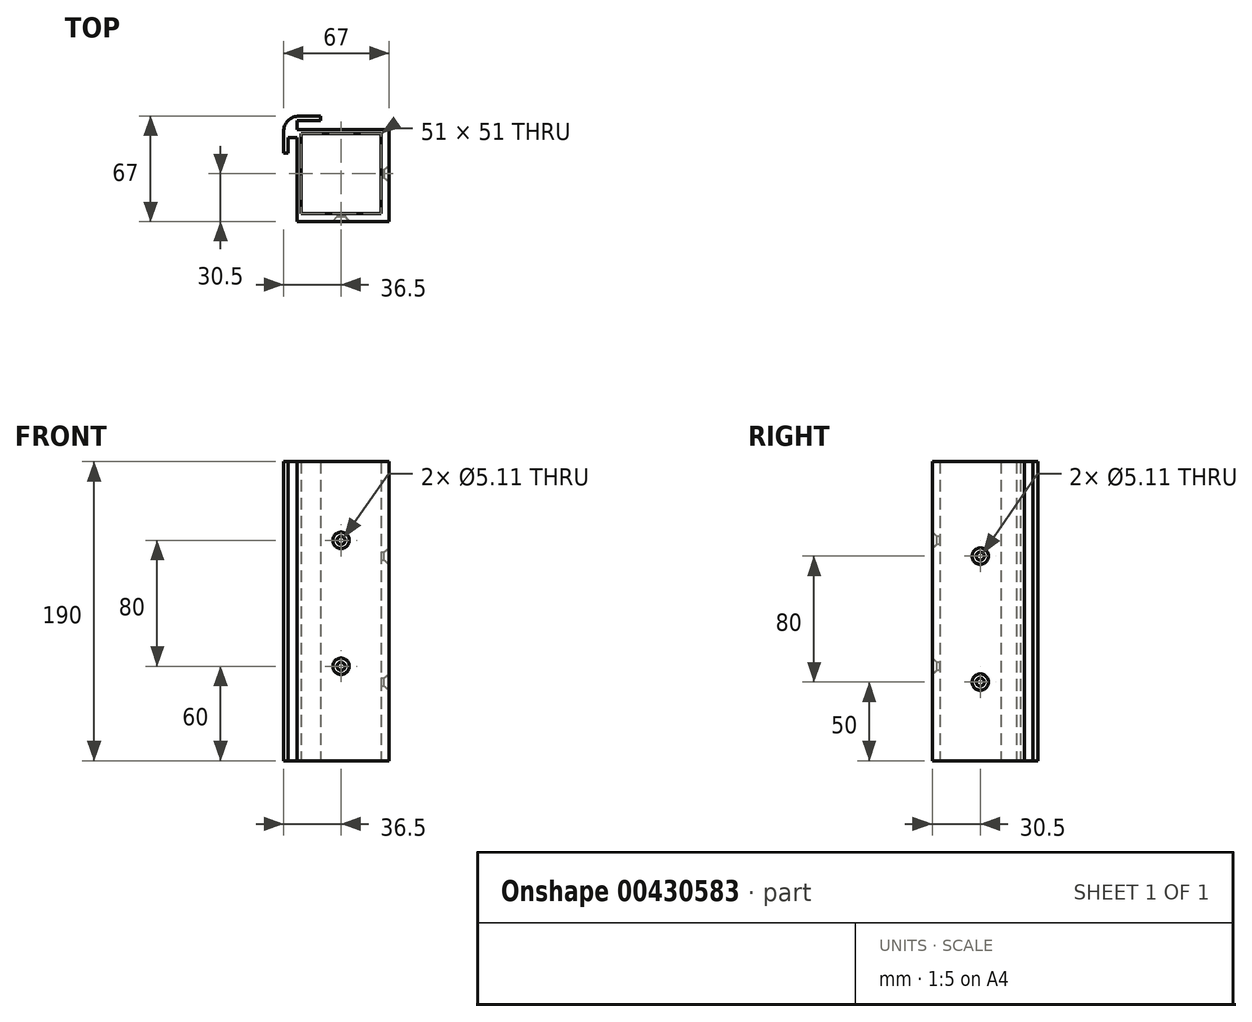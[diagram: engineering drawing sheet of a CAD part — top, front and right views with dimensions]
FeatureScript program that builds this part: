
annotation { "Feature Type Name" : "Feature", "Feature Type Description" : "" }
export const myFeature = defineFeature(function(context is Context, id is Id, definition is map)
    precondition{}
    {
        {
            var Q0;
            Q0=qCreatedBy(makeId("Top.planeOp"),FACE);
            var sketch = newSketch(context, id + "F0", { "sketchPlane" : qUnion([Q0])});
            skLineSegment(sketch, "E0.bottom", {"start": v(25.5, -25.5) * mm, "end": v(-25.5, -25.5) * mm});
            skLineSegment(sketch, "E0.top", {"start": v(25.5, 25.5) * mm, "end": v(-25.5, 25.5) * mm});
            skLineSegment(sketch, "E0.left", {"start": v(25.5, -25.5) * mm, "end": v(25.5, 25.5) * mm});
            skLineSegment(sketch, "E0.right", {"start": v(-25.5, -25.5) * mm, "end": v(-25.5, 25.5) * mm});
            skPoint(sketch, "E0.middle", {"position": v(0, 0) * mm});
            skLineSegment(sketch, "E1.bottom", {"start": v(-28, 28) * mm, "end": v(30.5, 28) * mm});
            skLineSegment(sketch, "E1.top", {"start": v(-28, -30.5) * mm, "end": v(30.5, -30.5) * mm});
            skLineSegment(sketch, "E1.left", {"start": v(-28, 28) * mm, "end": v(-28, -30.5) * mm});
            skLineSegment(sketch, "E1.right", {"start": v(30.5, 28) * mm, "end": v(30.5, -30.5) * mm});
            skLineSegment(sketch, "E2.bottom", {"start": v(-28, 28) * mm, "end": v(-23, 28) * mm});
            skLineSegment(sketch, "E2.top", {"start": v(-28, 33.5) * mm, "end": v(-23, 33.5) * mm});
            skLineSegment(sketch, "E2.left", {"start": v(-28, 28) * mm, "end": v(-28, 33.5) * mm});
            skLineSegment(sketch, "E2.right", {"start": v(-23, 28) * mm, "end": v(-23, 33.5) * mm});
            skLineSegment(sketch, "E3.bottom", {"start": v(-28, 28) * mm, "end": v(-33.5, 28) * mm});
            skLineSegment(sketch, "E3.top", {"start": v(-28, 23) * mm, "end": v(-33.5, 23) * mm});
            skLineSegment(sketch, "E3.left", {"start": v(-28, 28) * mm, "end": v(-28, 23) * mm});
            skLineSegment(sketch, "E3.right", {"start": v(-33.5, 28) * mm, "end": v(-33.5, 23) * mm});
            skLineSegment(sketch, "E4.bottom", {"start": v(-33.5, 28) * mm, "end": v(-36.5, 28) * mm});
            skLineSegment(sketch, "E4.top", {"start": v(-33.5, 13) * mm, "end": v(-36.5, 13) * mm});
            skLineSegment(sketch, "E4.left", {"start": v(-33.5, 28) * mm, "end": v(-33.5, 13) * mm});
            skLineSegment(sketch, "E4.right", {"start": v(-36.5, 28) * mm, "end": v(-36.5, 13) * mm});
            skLineSegment(sketch, "E5.bottom", {"start": v(-28, 33.5) * mm, "end": v(-13, 33.5) * mm});
            skLineSegment(sketch, "E5.top", {"start": v(-28, 36.5) * mm, "end": v(-13, 36.5) * mm});
            skLineSegment(sketch, "E5.left", {"start": v(-28, 33.5) * mm, "end": v(-28, 36.5) * mm});
            skLineSegment(sketch, "E5.right", {"start": v(-13, 33.5) * mm, "end": v(-13, 36.5) * mm});
            skLineSegment(sketch, "E6.bottom", {"start": v(-28, 28) * mm, "end": v(-36.5, 28) * mm});
            skLineSegment(sketch, "E6.top", {"start": v(-28, 36.5) * mm, "end": v(-36.5, 36.5) * mm});
            skLineSegment(sketch, "E6.left", {"start": v(-28, 28) * mm, "end": v(-28, 36.5) * mm});
            skLineSegment(sketch, "E6.right", {"start": v(-36.5, 28) * mm, "end": v(-36.5, 36.5) * mm});
            skSolve(sketch);
        }
        {
            var Q0;
            {var subQ4=sQuery(id+"F0.wireOp",EDGE,"E6.top");Q0=makeQuery(id+"F0.imprint","IMPRINT",FACE,{"disambiguationData":[TD([[makeQuery(id+"F0.imprint","IMPRINT",EDGE,{"derivedFrom":subQ4}),1.0]])]});}
            var Q1;
            {var subQ1=sQuery(id+"F0.wireOp",EDGE,"E5.top");Q1=makeQuery(id+"F0.imprint","IMPRINT",FACE,{"disambiguationData":[TD([[makeQuery(id+"F0.imprint","IMPRINT",EDGE,{"derivedFrom":subQ1}),-1.0]])]});}
            var Q2;
            {var subQ0=sQuery(id+"F0.wireOp",EDGE,"E2.bottom");Q2=makeQuery(id+"F0.imprint","IMPRINT",FACE,{"disambiguationData":[TD([[makeQuery(id+"F0.imprint","IMPRINT",EDGE,{"derivedFrom":subQ0}),1.0]])]});}
            var Q3;
            {var subQ0=sQuery(id+"F0.wireOp",EDGE,"E3.top");Q3=makeQuery(id+"F0.imprint","IMPRINT",FACE,{"disambiguationData":[TD([[makeQuery(id+"F0.imprint","IMPRINT",EDGE,{"derivedFrom":subQ0}),-1.0]])]});}
            var Q4;
            {var subQ3=sQuery(id+"F0.wireOp",EDGE,"E4.top");Q4=makeQuery(id+"F0.imprint","IMPRINT",FACE,{"disambiguationData":[TD([[makeQuery(id+"F0.imprint","IMPRINT",EDGE,{"derivedFrom":subQ3}),-1.0]])]});}
            var Q5;
            Q5=makeQuery(id+"F0.imprint","IMPRINT",FACE,{"disambiguationData":[TD([[makeQuery(id+"F0.imprint","IMPRINT",EDGE,{"derivedFrom":sQuery(id+"F0.wireOp",EDGE,"E0.bottom")}),1.0]])]});
            extrude(context, id + "F1", {"entities" : qUnion([Q0, Q1, Q2, Q3, Q4, Q5]), "depth" : 190 * mm, "offsetDistance" : 25 * mm});
        }
        {
            var Q0;
            Q0=makeQuery(id+"F1.opExtrude","SWEPT_EDGE",EDGE,{"disambiguationData":[OSD([sQuery(id+"F0.wireOp",EDGE,"E6.top"),sQuery(id+"F0.wireOp",EDGE,"E6.right")])]});
            fillet(context, id + "F2", {"entities" : qUnion([Q0]), "radius" : 10 * mm, "tangentPropagation" : true, "allowEdgeOverflow" : false});
        }
        {
            var Q0;
            Q0=makeQuery(id+"F1.opExtrude","SWEPT_FACE",FACE,{"disambiguationData":[OSD([sQuery(id+"F0.wireOp",EDGE,"E1.top")])]});
            var sketch = newSketch(context, id + "F3", { "sketchPlane" : qUnion([Q0])});
            skPoint(sketch, "E7", {"position": v(0, 140) * mm});
            skPoint(sketch, "E8", {"position": v(0, 60) * mm});
            skSolve(sketch);
        }
        {
            var Q0;
            Q0=sQuery(id+"F3.wireOp",VERTEX,"E7");
            var Q1;
            Q1=sQuery(id+"F3.wireOp",VERTEX,"E8");
            var Q2;
            Q2=makeQuery(id+"F1.opExtrude","SWEPT_BODY",BODY,{"disambiguationData":[OSD([sQuery(id+"F0.wireOp",EDGE,"E0.bottom"),sQuery(id+"F0.wireOp",EDGE,"E0.top"),sQuery(id+"F0.wireOp",EDGE,"E0.left"),sQuery(id+"F0.wireOp",EDGE,"E0.right"),sQuery(id+"F0.wireOp",EDGE,"E1.bottom"),sQuery(id+"F0.wireOp",EDGE,"E1.top"),sQuery(id+"F0.wireOp",EDGE,"E1.left"),sQuery(id+"F0.wireOp",EDGE,"E1.right"),sQuery(id+"F0.wireOp",EDGE,"E2.right"),sQuery(id+"F0.wireOp",EDGE,"E3.top"),sQuery(id+"F0.wireOp",EDGE,"E4.top"),sQuery(id+"F0.wireOp",EDGE,"E4.left"),sQuery(id+"F0.wireOp",EDGE,"E4.right"),sQuery(id+"F0.wireOp",EDGE,"E5.bottom"),sQuery(id+"F0.wireOp",EDGE,"E5.top"),sQuery(id+"F0.wireOp",EDGE,"E5.right"),sQuery(id+"F0.wireOp",EDGE,"E6.top"),sQuery(id+"F0.wireOp",EDGE,"E6.right")])]});
            hole(context, id + "F4", {"style" : HoleStyle.C_SINK, "endStyle" : HoleEndStyle.BLIND, "standardTappedOrClearance" : lookupTablePath({ "standard" : "ANSI", "fit" : "Normal (ASME)", "size" : "#10", "type" : "Clearance" }), "standardBlindInLast" : lookupTablePath({ "fit" : "Free", "standard" : "ANSI", "size" : "#10", "type" : "Clearance" }), "holeDiameter" : 5.1 * mm, "cSinkDiameter" : 10.44 * mm, "cSinkAngle" : 82 * degree, "majorDiameter" : 5 * mm, "holeDepth" : 12 * mm, "isTappedThrough" : true, "tappedDepth" : 12 * mm, "tapClearance" : 3, "locations" : qUnion([Q0, Q1]), "scope" : qUnion([Q2])});
        }
        {
            var Q0;
            Q0=makeQuery(id+"F1.opExtrude","SWEPT_FACE",FACE,{"disambiguationData":[OSD([sQuery(id+"F0.wireOp",EDGE,"E1.right")])]});
            var sketch = newSketch(context, id + "F5", { "sketchPlane" : qUnion([Q0])});
            skPoint(sketch, "E9", {"position": v(0, 130) * mm});
            skPoint(sketch, "E10", {"position": v(0, 50) * mm});
            skSolve(sketch);
        }
        {
            var Q0;
            Q0=sQuery(id+"F5.wireOp",VERTEX,"E9");
            var Q1;
            Q1=sQuery(id+"F5.wireOp",VERTEX,"E10");
            var Q2;
            Q2=makeQuery(id+"F1.opExtrude","SWEPT_BODY",BODY,{"disambiguationData":[OSD([sQuery(id+"F0.wireOp",EDGE,"E0.bottom"),sQuery(id+"F0.wireOp",EDGE,"E0.top"),sQuery(id+"F0.wireOp",EDGE,"E0.left"),sQuery(id+"F0.wireOp",EDGE,"E0.right"),sQuery(id+"F0.wireOp",EDGE,"E1.bottom"),sQuery(id+"F0.wireOp",EDGE,"E1.top"),sQuery(id+"F0.wireOp",EDGE,"E1.left"),sQuery(id+"F0.wireOp",EDGE,"E1.right"),sQuery(id+"F0.wireOp",EDGE,"E2.right"),sQuery(id+"F0.wireOp",EDGE,"E3.top"),sQuery(id+"F0.wireOp",EDGE,"E4.top"),sQuery(id+"F0.wireOp",EDGE,"E4.left"),sQuery(id+"F0.wireOp",EDGE,"E4.right"),sQuery(id+"F0.wireOp",EDGE,"E5.bottom"),sQuery(id+"F0.wireOp",EDGE,"E5.top"),sQuery(id+"F0.wireOp",EDGE,"E5.right"),sQuery(id+"F0.wireOp",EDGE,"E6.top"),sQuery(id+"F0.wireOp",EDGE,"E6.right")])]});
            hole(context, id + "F6", {"style" : HoleStyle.C_SINK, "endStyle" : HoleEndStyle.BLIND, "standardTappedOrClearance" : lookupTablePath({ "standard" : "ANSI", "fit" : "Normal (ASME)", "size" : "#10", "type" : "Clearance" }), "standardBlindInLast" : lookupTablePath({ "fit" : "Free", "standard" : "ANSI", "size" : "#10", "type" : "Clearance" }), "holeDiameter" : 5.1 * mm, "cSinkDiameter" : 10.44 * mm, "cSinkAngle" : 82 * degree, "holeDepth" : 12 * mm, "isTappedThrough" : true, "tappedDepth" : 12 * mm, "tapClearance" : 3, "locations" : qUnion([Q0, Q1]), "scope" : qUnion([Q2])});
        }
    });
